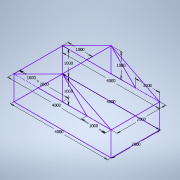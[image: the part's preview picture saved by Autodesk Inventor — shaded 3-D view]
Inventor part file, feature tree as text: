
AUTODESK INVENTOR PART (.ipt)
format: ipt  version: 2021 (Build 250183000, 183)  size: 106,496 bytes
history: native  units: mm
features: sketch x1
ambient origin geometry x8: Origin, YZ Plane, XZ Plane, XY Plane, X Axis, Y Axis, Z Axis, Center Point
feature tree (1):
  sketch  "Esboço 3D1"  dims[d0=4000.0mm d1=2000.0mm d2=4000.0mm d3=1000.0mm d4=4000.0mm d5=2000.0mm d6=4000.0mm d7=2000.0mm d8=1000.0mm d9=1000.0mm d10=1000.0mm d11=1000.0mm d12=1000.0mm d13=1000.0mm]
